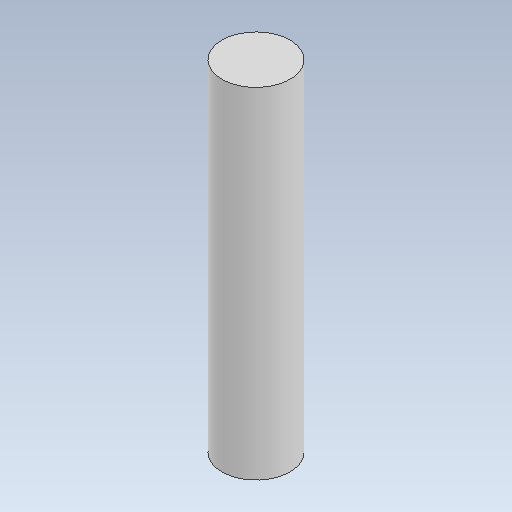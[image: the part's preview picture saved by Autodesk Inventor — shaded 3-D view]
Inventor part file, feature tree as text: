
AUTODESK INVENTOR PART (.ipt)
format: ipt  version: 2023 (Build 270158000, 158)  size: 76,800 bytes
history: native  units: mm
features: other x3, sketch x1
ambient origin geometry x8: Origin, YZ Plane, XZ Plane, XY Plane, X Axis, Y Axis, Z Axis, Center Point
bodies: Solid1 (feature_tree)
feature tree (4):
  other  "pin_3_15.ipt"
  other  "Solid1::pin_3_15.ipt"
  other  "TaggingFeature1"
  sketch  "Sketch1"  dims[d0=10.0mm]
